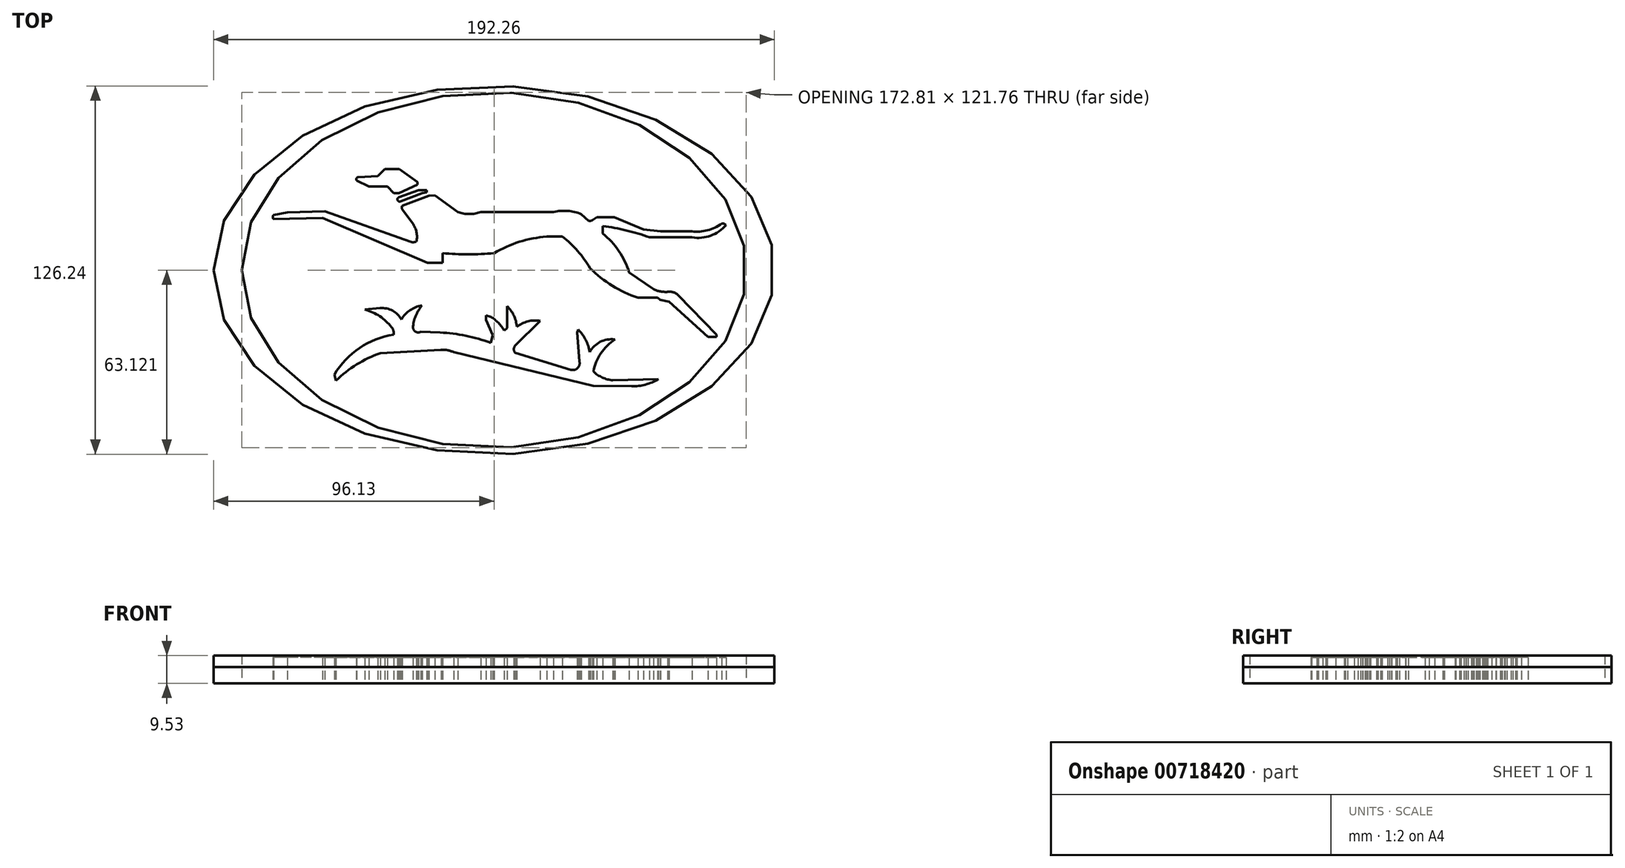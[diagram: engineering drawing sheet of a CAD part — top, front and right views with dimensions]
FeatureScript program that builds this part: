
annotation { "Feature Type Name" : "Feature", "Feature Type Description" : "" }
export const myFeature = defineFeature(function(context is Context, id is Id, definition is map)
    precondition{}
    {
        {
            var Q0;
            Q0=qCreatedBy(makeId("Top.planeOp"),FACE);
            var sketch = newSketch(context, id + "F0", { "sketchPlane" : qUnion([Q0])});
            skEllipse(sketch, "E0", {"center": v(0, 14.18) * mm, "majorRadius": 86.4 * mm, "minorRadius": 60.88 * mm, "majorAxis": v(-1, 0)});
            skEllipse(sketch, "E1", {"center": v(0, 14.18) * mm, "majorRadius": 96.13 * mm, "minorRadius": 63.12 * mm, "majorAxis": v(-1, 0)});
            skLineSegment(sketch, "E2", {"start": v(-37.44, 48.78) * mm, "end": v(-32.43, 48.78) * mm});
            skLineSegment(sketch, "E3", {"start": v(-32.43, 48.78) * mm, "end": v(-26.24, 44.4) * mm});
            skLineSegment(sketch, "E4", {"start": v(-26.24, 44.4) * mm, "end": v(-26.24, 43.54) * mm});
            skLineSegment(sketch, "E5", {"start": v(-26.24, 43.54) * mm, "end": v(-32.6, 40.54) * mm});
            skLineSegment(sketch, "E6", {"start": v(-32.6, 40.54) * mm, "end": v(-34.41, 40.54) * mm});
            skLineSegment(sketch, "E7", {"start": v(-34.41, 40.54) * mm, "end": v(-36.56, 42.86) * mm});
            skLineSegment(sketch, "E8", {"start": v(-36.56, 42.86) * mm, "end": v(-42.88, 42.86) * mm});
            skLineSegment(sketch, "E9", {"start": v(-42.88, 42.86) * mm, "end": v(-47.06, 44.87) * mm});
            skLineSegment(sketch, "E10", {"start": v(-37.44, 48.78) * mm, "end": v(-39.8, 46.46) * mm});
            skLineSegment(sketch, "E11", {"start": v(-39.8, 46.46) * mm, "end": v(-46.53, 46.02) * mm});
            skArc(sketch, "E12", {"start": v(-46.53, 46.02) * mm, "mid": v(-47.14, 45.6) * mm, "end": v(-47.06, 44.87) * mm});
            skArc(sketch, "E13", {"start": v(-32.64, 39.14) * mm, "mid": v(-33, 38.1) * mm, "end": v(-31.94, 37.8) * mm});
            skLineSegment(sketch, "E14", {"start": v(-32.64, 39.14) * mm, "end": v(-25.85, 41.53) * mm});
            skLineSegment(sketch, "E15", {"start": v(-25.85, 41.53) * mm, "end": v(-23.12, 41.53) * mm});
            skLineSegment(sketch, "E16", {"start": v(-23.12, 41.53) * mm, "end": v(-23.12, 40.8) * mm});
            skLineSegment(sketch, "E17", {"start": v(-23.12, 40.8) * mm, "end": v(-24.62, 40.55) * mm});
            skLineSegment(sketch, "E18", {"start": v(-24.62, 40.55) * mm, "end": v(-31.94, 37.8) * mm});
            skLineSegment(sketch, "E19", {"start": v(-22.34, 39.72) * mm, "end": v(-31.4, 36.3) * mm});
            skArc(sketch, "E20", {"start": v(-31.4, 36.3) * mm, "mid": v(-31.6, 35.62) * mm, "end": v(-31.4, 34.93) * mm});
            skLineSegment(sketch, "E21", {"start": v(-31.4, 34.93) * mm, "end": v(-27.92, 30.22) * mm});
            skArc(sketch, "E22", {"start": v(-26.57, 23.96) * mm, "mid": v(-26.57, 27.23) * mm, "end": v(-27.92, 30.22) * mm});
            skLineSegment(sketch, "E23", {"start": v(-57.95, 34.36) * mm, "end": v(-28.63, 23.89) * mm});
            skArc(sketch, "E24", {"start": v(-28.63, 23.89) * mm, "mid": v(-27.6, 23.73) * mm, "end": v(-26.57, 23.96) * mm});
            skLineSegment(sketch, "E25", {"start": v(-57.95, 34.36) * mm, "end": v(-70.76, 33.97) * mm});
            skLineSegment(sketch, "E26", {"start": v(-70.76, 33.97) * mm, "end": v(-75.56, 33.1) * mm});
            skLineSegment(sketch, "E27", {"start": v(-58.73, 32.1) * mm, "end": v(-75.6, 31.72) * mm});
            skArc(sketch, "E28", {"start": v(-75.56, 33.1) * mm, "mid": v(-75.77, 32.42) * mm, "end": v(-75.6, 31.72) * mm});
            skLineSegment(sketch, "E29", {"start": v(-58.73, 32.1) * mm, "end": v(-22.83, 16.7) * mm});
            skLineSegment(sketch, "E30", {"start": v(-22.83, 16.7) * mm, "end": v(-18.12, 16.7) * mm});
            skLineSegment(sketch, "E31", {"start": v(-18.12, 16.7) * mm, "end": v(-17.65, 16.72) * mm});
            skLineSegment(sketch, "E32", {"start": v(-17.65, 16.72) * mm, "end": v(-17.65, 20) * mm});
            skArc(sketch, "E33", {"start": v(-17.65, 20) * mm, "mid": v(-8.83, 19.57) * mm, "end": v(0, 20) * mm});
            skArc(sketch, "E34", {"start": v(18.07, 25.7) * mm, "mid": v(8.71, 23.87) * mm, "end": v(0, 20) * mm});
            skLineSegment(sketch, "E35", {"start": v(18.07, 25.7) * mm, "end": v(23.44, 25.7) * mm});
            skArc(sketch, "E36", {"start": v(32.9, 14.84) * mm, "mid": v(28.7, 20.73) * mm, "end": v(23.44, 25.7) * mm});
            skArc(sketch, "E37", {"start": v(32.9, 14.84) * mm, "mid": v(40.55, 8.86) * mm, "end": v(49.33, 4.69) * mm});
            skLineSegment(sketch, "E38", {"start": v(49.33, 4.69) * mm, "end": v(56.1, 4.69) * mm});
            skLineSegment(sketch, "E39", {"start": v(56.1, 4.69) * mm, "end": v(57.01, 3.94) * mm});
            skLineSegment(sketch, "E40", {"start": v(57.01, 3.94) * mm, "end": v(59.97, 3.35) * mm});
            skLineSegment(sketch, "E41", {"start": v(59.97, 3.35) * mm, "end": v(73.29, -8.74) * mm});
            skLineSegment(sketch, "E42", {"start": v(73.29, -8.74) * mm, "end": v(76.3, -8.74) * mm});
            skLineSegment(sketch, "E43", {"start": v(76.3, -8.74) * mm, "end": v(76.3, -7.99) * mm});
            skLineSegment(sketch, "E44", {"start": v(76.3, -7.99) * mm, "end": v(63.2, 5.5) * mm});
            skArc(sketch, "E45", {"start": v(63.2, 5.5) * mm, "mid": v(61.51, 6.55) * mm, "end": v(59.54, 6.73) * mm});
            skArc(sketch, "E46", {"start": v(54.65, 7.64) * mm, "mid": v(57.03, 6.87) * mm, "end": v(59.54, 6.73) * mm});
            skLineSegment(sketch, "E47", {"start": v(54.65, 7.64) * mm, "end": v(46.32, 13.4) * mm});
            skArc(sketch, "E48", {"start": v(46.32, 13.4) * mm, "mid": v(42.79, 20.71) * mm, "end": v(37.3, 26.71) * mm});
            skLineSegment(sketch, "E49", {"start": v(37.3, 26.71) * mm, "end": v(37.3, 29.29) * mm});
            skArc(sketch, "E50", {"start": v(53.3, 25.42) * mm, "mid": v(45.4, 27.78) * mm, "end": v(37.3, 29.29) * mm});
            skLineSegment(sketch, "E51", {"start": v(53.3, 25.42) * mm, "end": v(67.92, 25.42) * mm});
            skArc(sketch, "E52", {"start": v(67.92, 25.42) * mm, "mid": v(74.27, 26) * mm, "end": v(79.52, 29.61) * mm});
            skArc(sketch, "E53", {"start": v(67.9, 27.48) * mm, "mid": v(73.2, 27.83) * mm, "end": v(78.03, 30.09) * mm});
            skArc(sketch, "E54", {"start": v(79.52, 29.61) * mm, "mid": v(78.84, 30.06) * mm, "end": v(78.03, 30.09) * mm});
            skLineSegment(sketch, "E55", {"start": v(67.9, 27.48) * mm, "end": v(57.12, 27.48) * mm});
            skLineSegment(sketch, "E56", {"start": v(57.12, 27.48) * mm, "end": v(51.2, 28.15) * mm});
            skLineSegment(sketch, "E57", {"start": v(51.2, 28.15) * mm, "end": v(41.16, 32.26) * mm});
            skLineSegment(sketch, "E58", {"start": v(41.16, 32.26) * mm, "end": v(35.18, 32.26) * mm});
            skLineSegment(sketch, "E59", {"start": v(35.18, 32.26) * mm, "end": v(33.71, 31.28) * mm});
            skLineSegment(sketch, "E60", {"start": v(33.71, 31.28) * mm, "end": v(33.14, 30.98) * mm});
            skLineSegment(sketch, "E61", {"start": v(33.14, 30.98) * mm, "end": v(32.48, 30.98) * mm});
            skLineSegment(sketch, "E62", {"start": v(32.48, 30.98) * mm, "end": v(29.96, 33.38) * mm});
            skArc(sketch, "E63", {"start": v(29.96, 33.38) * mm, "mid": v(25.24, 34.48) * mm, "end": v(20.41, 34.1) * mm});
            skLineSegment(sketch, "E64", {"start": v(20.41, 34.1) * mm, "end": v(-4.5, 34.1) * mm});
            skArc(sketch, "E65", {"start": v(-12.42, 34.1) * mm, "mid": v(-8.46, 33.41) * mm, "end": v(-4.5, 34.1) * mm});
            skLineSegment(sketch, "E66", {"start": v(-12.42, 34.1) * mm, "end": v(-20.24, 39.85) * mm});
            skLineSegment(sketch, "E67", {"start": v(-20.24, 39.85) * mm, "end": v(-22.34, 39.72) * mm});
            skLineSegment(sketch, "E68", {"start": v(-18.25, -13.13) * mm, "end": v(-39, -14.26) * mm});
            skArc(sketch, "E69", {"start": v(-39, -14.26) * mm, "mid": v(-47.06, -18.18) * mm, "end": v(-54.13, -23.7) * mm});
            skLineSegment(sketch, "E70", {"start": v(-54.13, -23.7) * mm, "end": v(-54.72, -21.68) * mm});
            skArc(sketch, "E71", {"start": v(-34.38, -7.92) * mm, "mid": v(-46.09, -12.54) * mm, "end": v(-54.72, -21.68) * mm});
            skArc(sketch, "E72", {"start": v(-34.38, -7.92) * mm, "mid": v(-34.47, -6.58) * mm, "end": v(-35.08, -5.38) * mm});
            skArc(sketch, "E73", {"start": v(-35.08, -5.38) * mm, "mid": v(-39.16, -1.64) * mm, "end": v(-44.2, 0.64) * mm});
            skLineSegment(sketch, "E74", {"start": v(-44.2, 0.64) * mm, "end": v(-39.02, 1.13) * mm});
            skArc(sketch, "E75", {"start": v(-31.74, -2.77) * mm, "mid": v(-34.79, 0.28) * mm, "end": v(-39.02, 1.13) * mm});
            skArc(sketch, "E76", {"start": v(-24.7, 2.04) * mm, "mid": v(-28.77, 0.43) * mm, "end": v(-31.74, -2.77) * mm});
            skArc(sketch, "E77", {"start": v(-24.7, 2.04) * mm, "mid": v(-26.84, -1.55) * mm, "end": v(-27.77, -5.63) * mm});
            skArc(sketch, "E78", {"start": v(-27.77, -5.63) * mm, "mid": v(-26.75, -6.99) * mm, "end": v(-25.05, -6.95) * mm});
            skLineSegment(sketch, "E79", {"start": v(-25.05, -6.95) * mm, "end": v(-18.47, -7.23) * mm});
            skArc(sketch, "E80", {"start": v(-1.09, -10.78) * mm, "mid": v(-9.63, -8.31) * mm, "end": v(-18.47, -7.23) * mm});
            skLineSegment(sketch, "E81", {"start": v(-1.09, -10.78) * mm, "end": v(-0.5, -8.1) * mm});
            skLineSegment(sketch, "E82", {"start": v(-0.5, -8.1) * mm, "end": v(-2.72, -2.87) * mm});
            skLineSegment(sketch, "E83", {"start": v(-2.72, -2.87) * mm, "end": v(-2.72, -1.34) * mm});
            skLineSegment(sketch, "E84", {"start": v(-2.72, -1.34) * mm, "end": v(-1.09, -1.83) * mm});
            skArc(sketch, "E85", {"start": v(3.55, -6.6) * mm, "mid": v(1.52, -3.93) * mm, "end": v(-1.09, -1.83) * mm});
            skLineSegment(sketch, "E86", {"start": v(3.55, -6.6) * mm, "end": v(4.49, -5.7) * mm});
            skLineSegment(sketch, "E87", {"start": v(4.49, -5.7) * mm, "end": v(4.49, 1.83) * mm});
            skArc(sketch, "E88", {"start": v(7.83, -5.2) * mm, "mid": v(6.81, -1.38) * mm, "end": v(4.49, 1.83) * mm});
            skArc(sketch, "E89", {"start": v(15.8, -3.19) * mm, "mid": v(11.61, -3.4) * mm, "end": v(7.83, -5.2) * mm});
            skLineSegment(sketch, "E90", {"start": v(15.8, -3.19) * mm, "end": v(7.34, -11.65) * mm});
            skArc(sketch, "E91", {"start": v(7.34, -11.65) * mm, "mid": v(6.8, -12.94) * mm, "end": v(7.34, -14.23) * mm});
            skLineSegment(sketch, "E92", {"start": v(7.34, -14.23) * mm, "end": v(26.32, -19.98) * mm});
            skArc(sketch, "E93", {"start": v(26.32, -19.98) * mm, "mid": v(28.63, -19.43) * mm, "end": v(29.28, -17.15) * mm});
            skLineSegment(sketch, "E94", {"start": v(29.28, -17.15) * mm, "end": v(28.45, -7.23) * mm});
            skLineSegment(sketch, "E95", {"start": v(28.45, -7.23) * mm, "end": v(28.9, -6.22) * mm});
            skArc(sketch, "E96", {"start": v(32.77, -13.95) * mm, "mid": v(31.44, -9.78) * mm, "end": v(28.9, -6.22) * mm});
            skArc(sketch, "E97", {"start": v(41.4, -9.6) * mm, "mid": v(36.4, -10.43) * mm, "end": v(32.77, -13.95) * mm});
            skArc(sketch, "E98", {"start": v(41.4, -9.6) * mm, "mid": v(36.62, -14.33) * mm, "end": v(34.1, -20.57) * mm});
            skArc(sketch, "E99", {"start": v(34.1, -20.57) * mm, "mid": v(37.15, -22.66) * mm, "end": v(40.74, -23.56) * mm});
            skLineSegment(sketch, "E100", {"start": v(40.74, -23.56) * mm, "end": v(56.28, -23.21) * mm});
            skArc(sketch, "E101", {"start": v(47.22, -25.65) * mm, "mid": v(51.92, -25.07) * mm, "end": v(56.28, -23.21) * mm});
            skLineSegment(sketch, "E102", {"start": v(47.22, -25.65) * mm, "end": v(33.99, -25.43) * mm});
            skLineSegment(sketch, "E103", {"start": v(33.99, -25.43) * mm, "end": v(-13.83, -13.9) * mm});
            skArc(sketch, "E104", {"start": v(-13.83, -13.9) * mm, "mid": v(-16, -13.26) * mm, "end": v(-18.25, -13.13) * mm});
            skSolve(sketch);
        }
        {
            var Q0;
            Q0=makeQuery(id+"F0.imprint","IMPRINT",FACE,{"disambiguationData":[TD([[makeQuery(id+"F0.imprint","IMPRINT",EDGE,{"derivedFrom":sQuery(id+"F0.wireOp",EDGE,"E0")}),-1.0]])]});
            var Q1;
            Q1=makeQuery(id+"F0.imprint","IMPRINT",FACE,{"disambiguationData":[TD([[makeQuery(id+"F0.imprint","IMPRINT",EDGE,{"derivedFrom":sQuery(id+"F0.wireOp",EDGE,"E0")}),1.0]])]});
            var Q2;
            Q2=makeQuery(id+"F0.imprint","IMPRINT",FACE,{"disambiguationData":[TD([[makeQuery(id+"F0.imprint","IMPRINT",EDGE,{"derivedFrom":sQuery(id+"F0.wireOp",EDGE,"E2")}),-1.0]])]});
            var Q3;
            Q3=makeQuery(id+"F0.imprint","IMPRINT",FACE,{"disambiguationData":[TD([[makeQuery(id+"F0.imprint","IMPRINT",EDGE,{"derivedFrom":sQuery(id+"F0.wireOp",EDGE,"E13")}),1.0]])]});
            var Q4;
            Q4=makeQuery(id+"F0.imprint","IMPRINT",FACE,{"disambiguationData":[TD([[makeQuery(id+"F0.imprint","IMPRINT",EDGE,{"derivedFrom":sQuery(id+"F0.wireOp",EDGE,"E19")}),1.0]])]});
            var Q5;
            Q5=makeQuery(id+"F0.imprint","IMPRINT",FACE,{"disambiguationData":[TD([[makeQuery(id+"F0.imprint","IMPRINT",EDGE,{"derivedFrom":sQuery(id+"F0.wireOp",EDGE,"E68")}),-1.0]])]});
            extrude(context, id + "F1", {"entities" : qUnion([Q0, Q1, Q2, Q3, Q4, Q5]), "depth" : 5.6 * mm, "offsetDistance" : 25.4 * mm});
        }
        {
            var Q0;
            Q0=makeQuery(id+"F0.imprint","IMPRINT",FACE,{"disambiguationData":[TD([[makeQuery(id+"F0.imprint","IMPRINT",EDGE,{"derivedFrom":sQuery(id+"F0.wireOp",EDGE,"E0")}),-1.0]])]});
            extrude(context, id + "F2", {"entities" : qUnion([Q0]), "depth" : 9.52 * mm, "offsetDistance" : 25.4 * mm});
        }
        {
            var Q0;
            Q0=makeQuery(id+"F0.imprint","IMPRINT",FACE,{"disambiguationData":[TD([[makeQuery(id+"F0.imprint","IMPRINT",EDGE,{"derivedFrom":sQuery(id+"F0.wireOp",EDGE,"E2")}),-1.0]])]});
            var Q1;
            Q1=makeQuery(id+"F0.imprint","IMPRINT",FACE,{"disambiguationData":[TD([[makeQuery(id+"F0.imprint","IMPRINT",EDGE,{"derivedFrom":sQuery(id+"F0.wireOp",EDGE,"E13")}),1.0]])]});
            var Q2;
            Q2=makeQuery(id+"F0.imprint","IMPRINT",FACE,{"disambiguationData":[TD([[makeQuery(id+"F0.imprint","IMPRINT",EDGE,{"derivedFrom":sQuery(id+"F0.wireOp",EDGE,"E19")}),1.0]])]});
            var Q3;
            Q3=makeQuery(id+"F0.imprint","IMPRINT",FACE,{"disambiguationData":[TD([[makeQuery(id+"F0.imprint","IMPRINT",EDGE,{"derivedFrom":sQuery(id+"F0.wireOp",EDGE,"E68")}),-1.0]])]});
            extrude(context, id + "F3", {"entities" : qUnion([Q0, Q1, Q2, Q3]), "depth" : 8.9 * mm, "offsetDistance" : 25.4 * mm});
        }
    });
